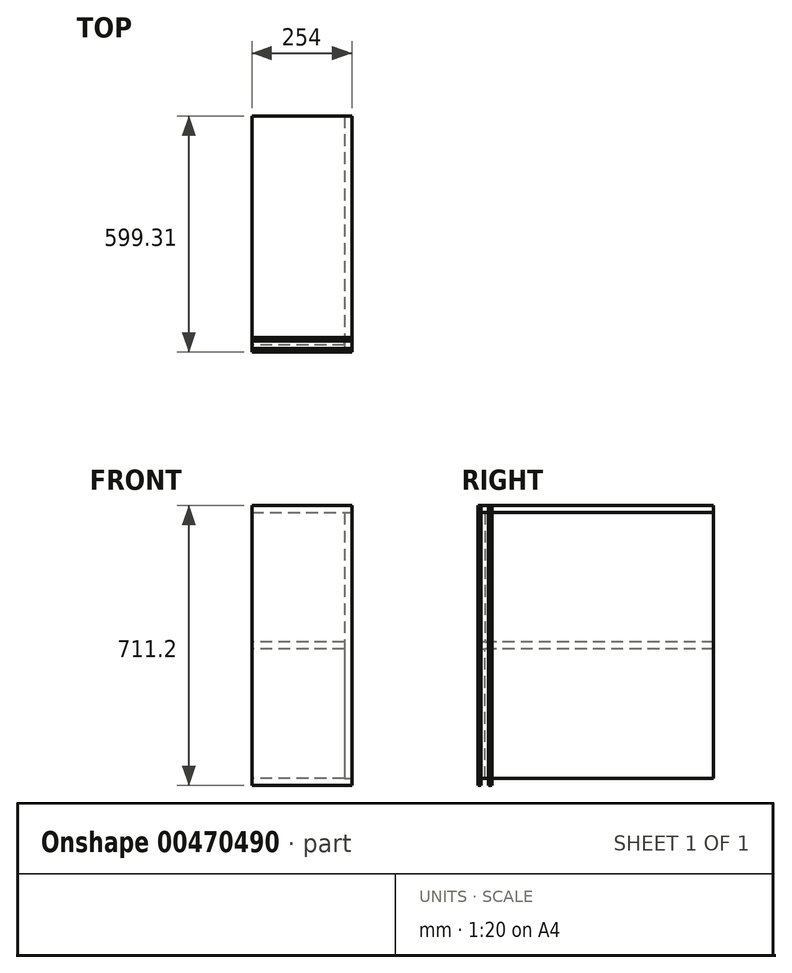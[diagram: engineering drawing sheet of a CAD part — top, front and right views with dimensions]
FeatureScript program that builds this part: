
annotation { "Feature Type Name" : "Feature", "Feature Type Description" : "" }
export const myFeature = defineFeature(function(context is Context, id is Id, definition is map)
    precondition{}
    {
        {
            var Q0;
            Q0=qCreatedBy(makeId("Front.planeOp"),FACE);
            var sketch = newSketch(context, id + "F0", { "sketchPlane" : qUnion([Q0])});
            skLineSegment(sketch, "E0.bottom", {"start": v(0, 0) * mm, "end": v(254, 0) * mm});
            skLineSegment(sketch, "E0.top", {"start": v(0, 711.2) * mm, "end": v(254, 711.2) * mm});
            skLineSegment(sketch, "E0.left", {"start": v(0, 0) * mm, "end": v(0, 711.2) * mm});
            skLineSegment(sketch, "E0.right", {"start": v(254, 0) * mm, "end": v(254, 711.2) * mm});
            skSolve(sketch);
        }
        {
            var Q0;
            Q0 = qSketchRegion(id + "F0", true);
            extrude(context, id + "F1", {"entities" : qUnion([Q0]), "depth" : 18.29 * mm, "offsetDistance" : 25.4 * mm});
        }
        {
            var Q0;
            Q0=makeQuery(id+"F1.opExtrude","SWEPT_FACE",FACE,{"disambiguationData":[OSD([sQuery(id+"F0.wireOp",EDGE,"E0.left")])]});
            var sketch = newSketch(context, id + "F2", { "sketchPlane" : qUnion([Q0])});
            skLineSegment(sketch, "E1.bottom", {"start": v(0, 711.2) * mm, "end": v(9.52, 711.2) * mm});
            skLineSegment(sketch, "E1.top", {"start": v(0, 692.91) * mm, "end": v(9.53, 692.91) * mm});
            skLineSegment(sketch, "E1.left", {"start": v(0, 711.2) * mm, "end": v(0, 692.91) * mm});
            skLineSegment(sketch, "E1.right", {"start": v(9.53, 711.2) * mm, "end": v(9.53, 692.91) * mm});
            skSolve(sketch);
        }
        {
            var Q0;
            Q0=makeQuery(id+"F2.imprint","IMPRINT",FACE,{"disambiguationData":[TD([[makeQuery(id+"F2.imprint","IMPRINT",EDGE,{"derivedFrom":sQuery(id+"F2.wireOp",EDGE,"E1.bottom")}),1.0]])]});
            var Q1;
            Q1=makeQuery(id+"F1.opExtrude","CAP_EDGE",EDGE,{"disambiguationData":[OSD([sQuery(id+"F0.wireOp",EDGE,"E0.top")])],"isStart":true});
            var Q2;
            Q2=makeQuery(id+"F1.opExtrude","CAP_EDGE",EDGE,{"disambiguationData":[OSD([sQuery(id+"F0.wireOp",EDGE,"E0.right")])],"isStart":true});
            var Q3;
            Q3=makeQuery(id+"F1.opExtrude","CAP_EDGE",EDGE,{"disambiguationData":[OSD([sQuery(id+"F0.wireOp",EDGE,"E0.bottom")])],"isStart":true});
            sweep(context, id + "F3", {"operationType" : NewBodyOperationType.REMOVE, "profiles" : qUnion([Q0]), "path" : qUnion([Q1, Q2, Q3])});
        }
        {
            var Q0;
            Q0=makeQuery(id+"F1.opExtrude","SWEPT_FACE",FACE,{"disambiguationData":[OSD([sQuery(id+"F0.wireOp",EDGE,"E0.left")])]});
            var sketch = newSketch(context, id + "F4", { "sketchPlane" : qUnion([Q0])});
            skLineSegment(sketch, "E2.bottom", {"start": v(9.52, 364.74) * mm, "end": v(0, 364.74) * mm});
            skLineSegment(sketch, "E2.top", {"start": v(9.52, 346.46) * mm, "end": v(0, 346.46) * mm});
            skLineSegment(sketch, "E2.left", {"start": v(9.52, 364.74) * mm, "end": v(9.52, 346.46) * mm});
            skPoint(sketch, "E2.middle", {"position": v(0, 355.6) * mm});
            skLineSegment(sketch, "E3", {"start": v(0, 364.74) * mm, "end": v(0, 346.46) * mm});
            skPoint(sketch, "E2.right.start.orphan", {"position": v(-9.53, 364.74) * mm});
            skPoint(sketch, "E4.orphan", {"position": v(-9.53, 346.46) * mm});
            skSolve(sketch);
        }
        {
            var Q0;
            Q0=makeQuery(id+"F4.imprint","IMPRINT",FACE,{"disambiguationData":[TD([[makeQuery(id+"F4.imprint","IMPRINT",EDGE,{"derivedFrom":sQuery(id+"F4.wireOp",EDGE,"E2.bottom")}),1.0]])]});
            var Q1;
            Q1=makeQuery(id+"F3.boolean.opBoolean","COPY",FACE,{"derivedFrom":makeQuery(id+"F3.opSweep","SWEPT_FACE",FACE,{"disambiguationData":[OSD([sQuery(id+"F0.wireOp",EDGE,"E0.right"),sQuery(id+"F2.wireOp",EDGE,"E1.top")])]})});
            extrude(context, id + "F5", {"entities" : qUnion([Q0]), "operationType" : NewBodyOperationType.REMOVE, "endBound" : BoundingType.UP_TO_SURFACE, "oppositeDirection" : true, "depth" : 25.4 * mm, "endBoundEntityFace" : qUnion([Q1]), "offsetDistance" : 25.4 * mm});
        }
        {
            var Q0;
            Q0=makeQuery(id+"F5.boolean.opBoolean","MERGE",FACE,{"derivedFrom":[makeQuery(id+"F3.boolean.opBoolean","COPY",FACE,{"derivedFrom":makeQuery(id+"F3.opSweep","SWEPT_FACE",FACE,{"disambiguationData":[OSD([sQuery(id+"F0.wireOp",EDGE,"E0.top"),sQuery(id+"F2.wireOp",EDGE,"E1.right")])]})}),makeQuery(id+"F5.opExtrude","SWEPT_FACE",FACE,{"disambiguationData":[OSD([sQuery(id+"F4.wireOp",EDGE,"E2.left")])]})]});
            var sketch = newSketch(context, id + "F6", { "sketchPlane" : qUnion([Q0])});
            skLineSegment(sketch, "E5.bottom", {"start": v(0, 711.2) * mm, "end": v(-254, 711.2) * mm});
            skLineSegment(sketch, "E5.top", {"start": v(0, 692.91) * mm, "end": v(-254, 692.91) * mm});
            skLineSegment(sketch, "E5.left", {"start": v(0, 711.2) * mm, "end": v(0, 692.91) * mm});
            skLineSegment(sketch, "E5.right", {"start": v(-254, 711.2) * mm, "end": v(-254, 692.91) * mm});
            skSolve(sketch);
        }
        {
            var Q0;
            Q0=makeQuery(id+"F6.imprint","IMPRINT",FACE,{"disambiguationData":[TD([[makeQuery(id+"F6.imprint","IMPRINT",EDGE,{"derivedFrom":sQuery(id+"F6.wireOp",EDGE,"E5.bottom")}),1.0]])]});
            extrude(context, id + "F7", {"entities" : qUnion([Q0]), "depth" : 590.55 * mm, "offsetDistance" : 25.4 * mm});
        }
        {
            var Q0;
            Q0=makeQuery(id+"F5.boolean.opBoolean","MERGE",FACE,{"derivedFrom":[makeQuery(id+"F3.boolean.opBoolean","COPY",FACE,{"derivedFrom":makeQuery(id+"F3.opSweep","SWEPT_FACE",FACE,{"disambiguationData":[OSD([sQuery(id+"F0.wireOp",EDGE,"E0.top"),sQuery(id+"F2.wireOp",EDGE,"E1.right")])]})}),makeQuery(id+"F5.opExtrude","SWEPT_FACE",FACE,{"disambiguationData":[OSD([sQuery(id+"F4.wireOp",EDGE,"E2.left")])]})]});
            var sketch = newSketch(context, id + "F8", { "sketchPlane" : qUnion([Q0])});
            skLineSegment(sketch, "E6.bottom", {"start": v(-235.71, 692.91) * mm, "end": v(-254, 692.91) * mm});
            skLineSegment(sketch, "E6.top", {"start": v(-235.71, 18.29) * mm, "end": v(-254, 18.29) * mm});
            skLineSegment(sketch, "E6.left", {"start": v(-235.71, 692.91) * mm, "end": v(-235.71, 18.29) * mm});
            skLineSegment(sketch, "E6.right", {"start": v(-254, 692.91) * mm, "end": v(-254, 18.29) * mm});
            skSolve(sketch);
        }
        {
            var Q0;
            {var subQ1=sQuery(id+"F8.wireOp",EDGE,"E6.bottom");Q0=makeQuery(id+"F8.imprint","IMPRINT",FACE,{"disambiguationData":[TD([[makeQuery(id+"F8.imprint","IMPRINT",EDGE,{"derivedFrom":subQ1}),1.0]])]});}
            var Q1;
            Q1=makeQuery(id+"F7.opExtrude","CAP_FACE",FACE,{"disambiguationData":[OSD([sQuery(id+"F6.wireOp",EDGE,"E5.bottom"),sQuery(id+"F6.wireOp",EDGE,"E5.top"),sQuery(id+"F6.wireOp",EDGE,"E5.left"),sQuery(id+"F6.wireOp",EDGE,"E5.right")])],"isStart":false});
            extrude(context, id + "F9", {"entities" : qUnion([Q0]), "endBound" : BoundingType.UP_TO_SURFACE, "depth" : 25.4 * mm, "endBoundEntityFace" : qUnion([Q1]), "offsetDistance" : 25.4 * mm});
        }
        {
            var Q0;
            Q0=makeQuery(id+"F5.boolean.opBoolean","MERGE",FACE,{"derivedFrom":[makeQuery(id+"F3.boolean.opBoolean","COPY",FACE,{"derivedFrom":makeQuery(id+"F3.opSweep","SWEPT_FACE",FACE,{"disambiguationData":[OSD([sQuery(id+"F0.wireOp",EDGE,"E0.top"),sQuery(id+"F2.wireOp",EDGE,"E1.right")])]})}),makeQuery(id+"F5.opExtrude","SWEPT_FACE",FACE,{"disambiguationData":[OSD([sQuery(id+"F4.wireOp",EDGE,"E2.left")])]})]});
            var sketch = newSketch(context, id + "F10", { "sketchPlane" : qUnion([Q0])});
            skLineSegment(sketch, "E7.bottom", {"start": v(-235.71, 364.74) * mm, "end": v(0, 364.74) * mm});
            skLineSegment(sketch, "E7.top", {"start": v(-235.71, 346.46) * mm, "end": v(0, 346.46) * mm});
            skLineSegment(sketch, "E7.left", {"start": v(-235.71, 364.74) * mm, "end": v(-235.71, 346.46) * mm});
            skLineSegment(sketch, "E7.right", {"start": v(0, 364.74) * mm, "end": v(0, 346.46) * mm});
            skSolve(sketch);
        }
        {
            var Q0;
            Q0=makeQuery(id+"F10.imprint","IMPRINT",FACE,{"disambiguationData":[TD([[makeQuery(id+"F10.imprint","IMPRINT",EDGE,{"derivedFrom":sQuery(id+"F10.wireOp",EDGE,"E7.bottom")}),-1.0]])]});
            var Q1;
            Q1=makeQuery(id+"F7.opExtrude","CAP_FACE",FACE,{"disambiguationData":[OSD([sQuery(id+"F6.wireOp",EDGE,"E5.bottom"),sQuery(id+"F6.wireOp",EDGE,"E5.top"),sQuery(id+"F6.wireOp",EDGE,"E5.left"),sQuery(id+"F6.wireOp",EDGE,"E5.right")])],"isStart":false});
            extrude(context, id + "F11", {"entities" : qUnion([Q0]), "endBound" : BoundingType.UP_TO_SURFACE, "depth" : 25.4 * mm, "endBoundEntityFace" : qUnion([Q1]), "offsetDistance" : 25.4 * mm});
        }
        {
            var Q0;
            Q0=makeQuery(id+"F1.opExtrude","SWEPT_BODY",BODY,{"disambiguationData":[OSD([sQuery(id+"F0.wireOp",EDGE,"E0.bottom"),sQuery(id+"F0.wireOp",EDGE,"E0.top"),sQuery(id+"F0.wireOp",EDGE,"E0.left"),sQuery(id+"F0.wireOp",EDGE,"E0.right")])]});
            var Q1;
            Q1=qCreatedBy(makeId("Front.planeOp"),FACE);
            mirror(context, id + "F12", {"entities" : qUnion([Q0]), "mirrorPlane" : qUnion([Q1])});
        }
    });
